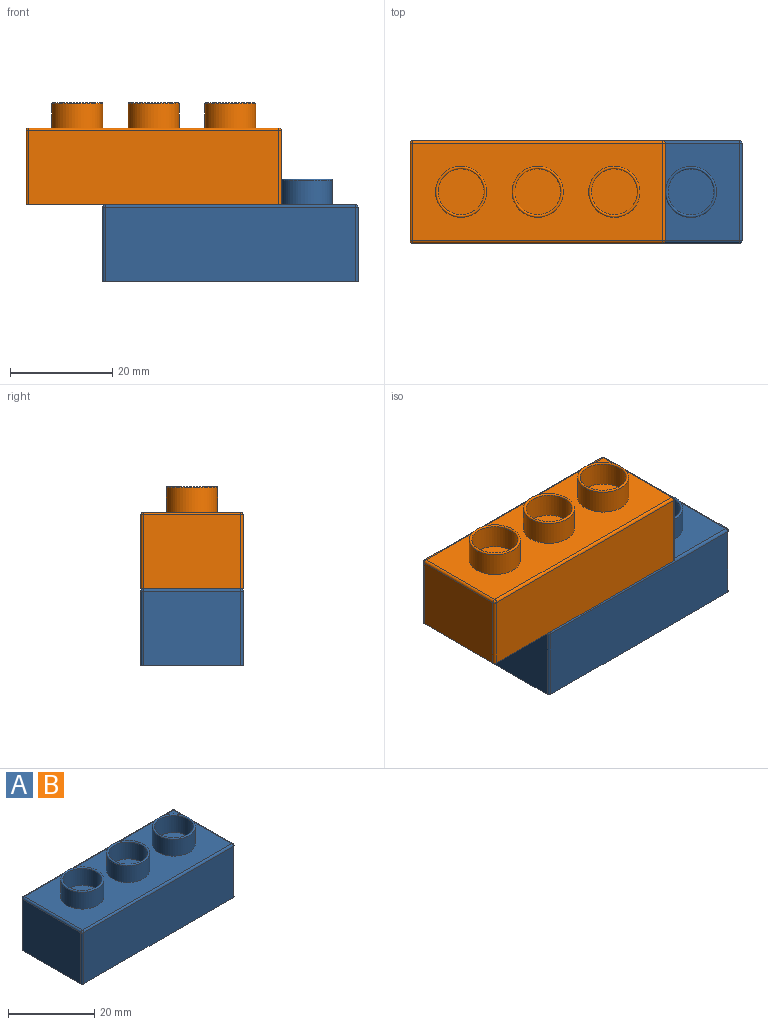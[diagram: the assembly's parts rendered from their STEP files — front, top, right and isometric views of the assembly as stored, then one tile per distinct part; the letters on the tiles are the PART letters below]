
ASSEMBLY  parts=2 mates=1
PART A: 84 faces, bbox 50x20x20 mm
  f0: plane 3.52x1mm, normal (0,0,-1), area 3.5mm2, adj f1,f2,f32,f44
  f1: plane 7x3.52mm, normal (-1,0,0), area 24.7mm2, adj f0,f32,f44,f49
  f2: plane 7x3.52mm, normal (1,0,0), area 24.7mm2, adj f0,f32,f35,f44
  f3: plane 7x3.52mm, normal (0,-1,0), area 24.7mm2, adj f5,f30,f39,f41
  f4: plane 7x3.52mm, normal (0,1,0), area 24.7mm2, adj f5,f30,f38,f41
  f5: plane 3.52x1mm, normal (0,0,-1), area 3.5mm2, adj f3,f4,f30,f41
  f6: plane 7x3.52mm, normal (-1,0,0), area 24.7mm2, adj f8,f37,f44,f53
  f7: plane 7x3.52mm, normal (1,0,0), area 24.7mm2, adj f8,f36,f44,f53
  f8: plane 3.52x1mm, normal (0,0,-1), area 3.5mm2, adj f6,f7,f44,f53
  f9: plane 7x4.05mm, normal (0,-1,0), area 28.3mm2, adj f11,f35,f44,f47
  f10: plane 7x4.05mm, normal (0,1,0), area 28.3mm2, adj f11,f36,f44,f47
  f11: plane 4.05x1mm, normal (0,0,-1), area 4mm2, adj f9,f10,f44,f47
  f12: plane 7x3.52mm, normal (0,-1,0), area 24.7mm2, adj f14,f31,f44,f49
  f13: plane 7x3.52mm, normal (0,1,0), area 24.7mm2, adj f14,f31,f37,f44
  f14: plane 3.52x1mm, normal (0,0,-1), area 3.5mm2, adj f12,f13,f31,f44
  f15: plane 7x3.52mm, normal (1,0,0), area 24.7mm2, adj f17,f32,f39,f41
  f16: plane 7x3.52mm, normal (-1,0,0), area 24.7mm2, adj f17,f32,f34,f41
  f17: plane 3.52x1mm, normal (0,0,-1), area 3.5mm2, adj f15,f16,f32,f41
  f18: plane 7x4.05mm, normal (0,-1,0), area 28.3mm2, adj f20,f34,f41,f47
  f19: plane 7x4.05mm, normal (0,1,0), area 28.3mm2, adj f20,f33,f41,f47
  f20: plane 4.05x1mm, normal (0,0,-1), area 4mm2, adj f18,f19,f41,f47
  f21: plane 7x3.52mm, normal (1,0,0), area 24.7mm2, adj f23,f32,f34,f47
  f22: plane 7x3.52mm, normal (-1,0,0), area 24.7mm2, adj f23,f32,f35,f47
  f23: plane 3.52x1mm, normal (0,0,-1), area 3.5mm2, adj f21,f22,f32,f47
  f24: plane 7x3.52mm, normal (-1,0,0), area 24.7mm2, adj f26,f36,f47,f53
  f25: plane 7x3.52mm, normal (1,0,0), area 24.7mm2, adj f26,f33,f47,f53
  f26: plane 3.52x1mm, normal (0,0,-1), area 3.5mm2, adj f24,f25,f47,f53
  f27: plane 7x3.52mm, normal (1,0,0), area 24.7mm2, adj f29,f38,f41,f53
  f28: plane 7x3.52mm, normal (-1,0,0), area 24.7mm2, adj f29,f33,f41,f53
  f29: plane 3.52x1mm, normal (0,0,-1), area 3.5mm2, adj f27,f28,f41,f53
  f30: plane 18x14mm, normal (-1,0,0), area 245mm2, adj f3,f4,f5,f32,f38,f39,f53,f67
  f31: plane 18x14mm, normal (1,0,0), area 245mm2, adj f12,f13,f14,f32,f37,f49,f53,f67
  f32: plane 48x14mm, normal (0,1,0), area 651mm2, adj f0,f1,f2,f15,f16,f17,f21,f22
  f33: plane 14x8.5mm, normal (0,0,-1), area 82mm2, adj f19,f25,f28,f41,f47,f53
  f34: plane 14x8.5mm, normal (0,0,-1), area 82mm2, adj f16,f18,f21,f32,f41,f47
  f35: plane 14x8.5mm, normal (0,0,-1), area 82mm2, adj f2,f9,f22,f32,f44,f47
  f36: plane 14x8.5mm, normal (0,0,-1), area 82mm2, adj f7,f10,f24,f44,f47,f53
  f37: plane 8.5x8.5mm, normal (0,0,-1), area 53.7mm2, adj f6,f13,f31,f44,f53
  f38: plane 8.5x8.5mm, normal (0,0,-1), area 53.7mm2, adj f4,f27,f30,f41,f53
  f39: plane 8.5x8.5mm, normal (0,0,-1), area 53.7mm2, adj f3,f15,f30,f32,f41
  f40: cylinder r=5mm len=14mm, axis (0,0,-1), area 439.8mm2, adj f42,f52
  f41: cylinder r=5.5mm len=14mm, axis (0,0,-1), area 455.8mm2, adj f3,f4,f5,f15,f16,f17,f18,f19
  f42: plane 11x11mm, normal (0,0,-1), area 16.5mm2, adj f40,f41
  f43: cylinder r=5mm len=14mm, axis (0,0,-1), area 439.8mm2, adj f45,f51
  f44: cylinder r=5.5mm len=14mm, axis (0,0,-1), area 455.8mm2, adj f0,f1,f2,f6,f7,f8,f9,f10
  f45: plane 11x11mm, normal (0,0,-1), area 16.5mm2, adj f43,f44
  f46: cylinder r=5mm len=14mm, axis (0,0,-1), area 439.8mm2, adj f48,f50
  f47: cylinder r=5.5mm len=14mm, axis (0,0,-1), area 455.8mm2, adj f9,f10,f11,f18,f19,f20,f21,f22
  f48: plane 11x11mm, normal (0,0,-1), area 16.5mm2, adj f46,f47
  f49: plane 8.5x8.5mm, normal (0,0,-1), area 53.7mm2, adj f1,f12,f31,f32,f44
  f50: plane 10x10mm, normal (0,0,-1), area 78.5mm2, adj f46
  f51: plane 10x10mm, normal (0,0,-1), area 78.5mm2, adj f43
  f52: plane 10x10mm, normal (0,0,-1), area 78.5mm2, adj f40
  f53: plane 48x14mm, normal (0,-1,0), area 651mm2, adj f6,f7,f8,f24,f25,f26,f27,f28
  f54: sphere r=0.5mm, area 0.4mm2, adj f56,f63,f65
  f55: sphere r=0.5mm, area 0.4mm2, adj f56,f60,f64
  f56: cylinder r=0.5mm len=49mm, axis (1,0,0), area 38.5mm2, adj f54,f55,f66,f69
  f57: sphere r=0.5mm, area 0.4mm2, adj f58,f61,f63
  f58: cylinder r=0.5mm len=14.5mm, axis (0,0,-1), area 11.4mm2, adj f57,f67,f82,f83
  f59: sphere r=0.5mm, area 0.4mm2, adj f60,f61,f62
  f60: cylinder r=0.5mm len=19mm, axis (0,-1,0), area 14.9mm2, adj f55,f59,f68,f69
  f61: cylinder r=0.5mm len=49mm, axis (-1,0,0), area 38.5mm2, adj f57,f59,f69,f83
  f62: cylinder r=0.5mm len=14.5mm, axis (0,0,1), area 11.4mm2, adj f59,f67,f68,f83
  f63: cylinder r=0.5mm len=19mm, axis (0,1,0), area 14.9mm2, adj f54,f57,f69,f82
  f64: cylinder r=0.5mm len=14.5mm, axis (0,0,1), area 11.4mm2, adj f55,f66,f67,f68
  f65: cylinder r=0.5mm len=14.5mm, axis (0,0,1), area 11.4mm2, adj f54,f66,f67,f82
  f66: plane 49x14.5mm, normal (0,1,0), area 710.5mm2, adj f56,f64,f65,f67
  f67: plane 50x20mm, normal (0,0,-1), area 135.8mm2, adj f30,f31,f32,f53,f58,f62,f64,f65
  f68: plane 19x14.5mm, normal (1,0,0), area 275.5mm2, adj f60,f62,f64,f67
  f69: plane 49x19mm, normal (0,0,1), area 695.4mm2, adj f56,f60,f61,f63,f72,f73,f78
  f70: cylinder r=4.5mm len=9mm, axis (0,0,-1), area 134.3mm2, adj f71,f81
  f71: torus R=4.75mm, axis (0,0,1), area 23.4mm2, adj f70,f72
  f72: cylinder r=5mm len=10mm, axis (0,0,-1), area 149.2mm2, adj f69,f71
  f73: cylinder r=5mm len=10mm, axis (0,0,-1), area 149.2mm2, adj f69,f74
  f74: torus R=4.75mm, axis (0,0,-1), area 23.4mm2, adj f73,f75
  f75: cylinder r=4.5mm len=9mm, axis (0,0,-1), area 134.3mm2, adj f74,f79
  f76: cylinder r=4.5mm len=9mm, axis (0,0,-1), area 134.3mm2, adj f77,f80
  f77: torus R=4.75mm, axis (0,0,1), area 23.4mm2, adj f76,f78
  f78: cylinder r=5mm len=10mm, axis (0,0,-1), area 149.2mm2, adj f69,f77
  f79: plane 9x9mm, normal (0,0,1), area 63.6mm2, adj f75
  f80: plane 9x9mm, normal (0,0,1), area 63.6mm2, adj f76
  f81: plane 9x9mm, normal (0,0,1), area 63.6mm2, adj f70
  f82: plane 19x14.5mm, normal (-1,0,0), area 275.5mm2, adj f58,f63,f65,f67
  f83: plane 49x14.5mm, normal (0,-1,0), area 710.5mm2, adj f58,f61,f62,f67
PART B: same geometry as A
PLACE A t=(2.32,12.65,0)mm
PLACE B t=(-12.68,12.65,15)mm
MATE slider B.f40 <-> A.f46  axis (0,0,-1) through (-22.68,22.65,15)mm
